# Revit family: EP_EOP_220-265
name_source: partatom
category: Structural Framing
revit_build: Autodesk Revit 2018 (Build: 20170223_1515(x64)
units: mm (PartAtom-declared; Revit-internal decimal feet)

## family parameters
Always export as geometry = No
Always vertical = Yes
Cut with Voids When Loaded = No
Display in Hidden Views = Edges Hidden by Other Members
Material for Model Behavior = Precast Concrete
Section Shape = Not Defined
Shared = No
Show family pre-cut in plan views = Yes
Structural Framing Length Roundoff = 1 mm

## types (2) — shared parameters
Fb_tugevusklass = C45/55

## per-type parameters (varying)
| type | Core Offset | Core Radius | H_kõrgus | Number Of Cores | TN_tunnus |
| EP6/220 | 126 mm | 75 mm | 220 mm  [stored 0.721785 ft] | 6 | vahelaeõõnespaneel |
| EP5/265 | 154 mm  [stored 0.505249 ft] | 93 mm | 265 mm  [stored 0.869423 ft] | 5 | õõnespaneel |

note: [stored X ft] marks values corroborated as IEEE doubles in the binary element streams (Revit-internal decimal feet)

## geometry (parser evidence)
native form markers: Sweep x14
no freeform markers — native parametric forms only
